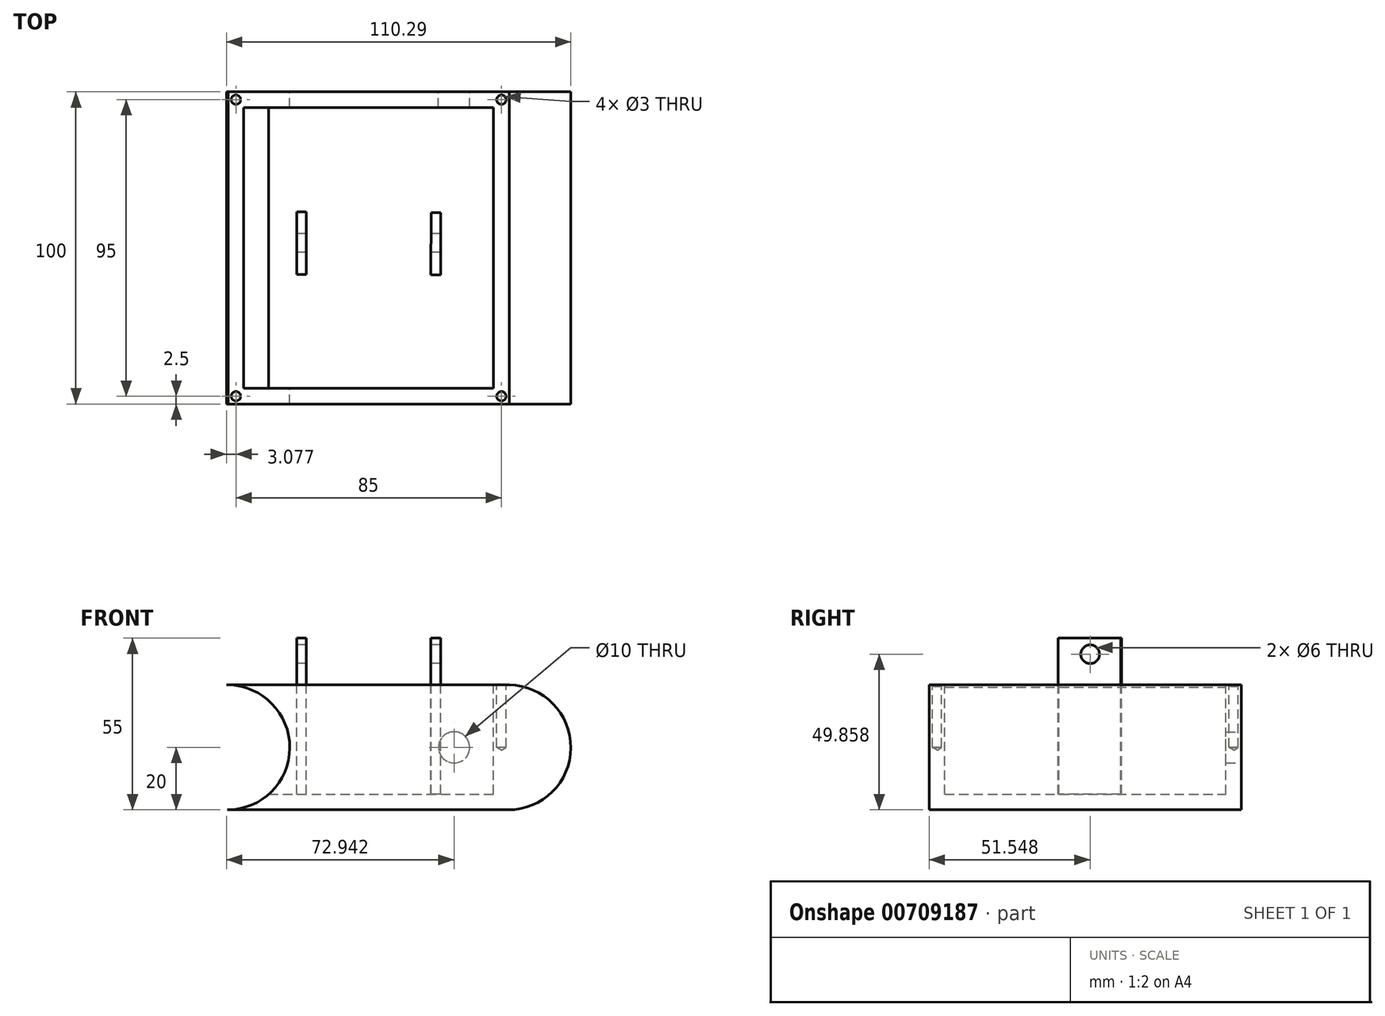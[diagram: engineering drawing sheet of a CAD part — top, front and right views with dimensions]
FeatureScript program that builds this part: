
annotation { "Feature Type Name" : "Feature", "Feature Type Description" : "" }
export const myFeature = defineFeature(function(context is Context, id is Id, definition is map)
    precondition{}
    {
        {
            var Q0;
            Q0=qCreatedBy(makeId("Front.planeOp"),FACE);
            var sketch = newSketch(context, id + "F0", { "sketchPlane" : qUnion([Q0])});
            skCircle(sketch, "E0", {"center": v(-60, 0) * mm, "radius": 20 * mm});
            skCircle(sketch, "E1", {"center": v(30, 0) * mm, "radius": 20 * mm});
            skLineSegment(sketch, "E2.top", {"start": v(-60.29, 20) * mm, "end": v(30.29, 20) * mm});
            skLineSegment(sketch, "E3", {"start": v(-60, -20) * mm, "end": v(30, -20) * mm});
            skSolve(sketch);
        }
        {
            var Q0;
            {var subQ0=sQuery(id+"F0.wireOp",EDGE,"E0");var subQ1=makeQuery(id+"F0.imprint","INTERSECT",VERTEX,{"derivedFrom":[subQ0,sQuery(id+"F0.wireOp",EDGE,"E2.top")]});Q0=makeQuery(id+"F0.imprint","IMPRINT",FACE,{"disambiguationData":[TD([[makeQuery(id+"F0.imprint","IMPRINT",EDGE,{"disambiguationData":[TD([[subQ1,-1.0]])],"derivedFrom":subQ0}),1.0]])]});}
            var Q1;
            {var subQ0=sQuery(id+"F0.wireOp",EDGE,"E1");var subQ1=makeQuery(id+"F0.imprint","INTERSECT",VERTEX,{"derivedFrom":[subQ0,sQuery(id+"F0.wireOp",EDGE,"3f78844c-1957-4825-8c51-001e57db5ed20.MirrorCS")]});Q1=makeQuery(id+"F0.imprint","IMPRINT",FACE,{"disambiguationData":[TD([[makeQuery(id+"F0.imprint","IMPRINT",EDGE,{"disambiguationData":[TD([[subQ1,1.0]])],"derivedFrom":subQ0}),1.0]])]});}
            var Q2;
            {var subQ3=sQuery(id+"F0.wireOp",EDGE,"E3");Q2=makeQuery(id+"F0.imprint","IMPRINT",FACE,{"disambiguationData":[TD([[makeQuery(id+"F0.imprint","IMPRINT",EDGE,{"derivedFrom":subQ3}),1.0]])]});}
            var Q3;
            {var subQ0=sQuery(id+"F0.wireOp",EDGE,"E2.top");var subQ1=sQuery(id+"F0.wireOp",EDGE,"E0");var subQ2=makeQuery(id+"F0.imprint","INTERSECT",VERTEX,{"disambiguationData":[OD(0.0)],"derivedFrom":[subQ1,subQ0]});Q3=makeQuery(id+"F0.imprint","IMPRINT",FACE,{"disambiguationData":[TD([[makeQuery(id+"F0.imprint","IMPRINT",EDGE,{"disambiguationData":[TD([[subQ2,-1.0]])],"derivedFrom":subQ1}),1.0]])]});}
            extrude(context, id + "F1", {"entities" : qUnion([Q0, Q1, Q2, Q3]), "endBound" : BoundingType.SYMMETRIC, "depth" : 100 * mm, "offsetDistance" : 25 * mm});
        }
        {
            var Q0;
            Q0=makeQuery(id+"F1.opExtrude","SWEPT_FACE",FACE,{"disambiguationData":[OSD([sQuery(id+"F0.wireOp",EDGE,"E2.top")])]});
            var sketch = newSketch(context, id + "F2", { "sketchPlane" : qUnion([Q0])});
            skLineSegment(sketch, "E4.bottom", {"start": v(-59.71, 50) * mm, "end": v(30.29, 50) * mm});
            skLineSegment(sketch, "E4.top", {"start": v(-59.71, -50) * mm, "end": v(30.29, -50) * mm});
            skLineSegment(sketch, "E4.left", {"start": v(-59.71, 50) * mm, "end": v(-59.71, -50) * mm});
            skLineSegment(sketch, "E4.right", {"start": v(30.29, 50) * mm, "end": v(30.29, -50) * mm});
            skLineSegment(sketch, "E5.bottom", {"start": v(-54.71, 45) * mm, "end": v(25.29, 45) * mm});
            skLineSegment(sketch, "E5.top", {"start": v(-54.71, -45) * mm, "end": v(25.29, -45) * mm});
            skLineSegment(sketch, "E5.left", {"start": v(-54.71, 45) * mm, "end": v(-54.71, -45) * mm});
            skLineSegment(sketch, "E5.right", {"start": v(25.29, 45) * mm, "end": v(25.29, -45) * mm});
            skLineSegment(sketch, "E6", {"start": v(-59.71, 50) * mm, "end": v(-54.71, 45) * mm});
            skLineSegment(sketch, "E7", {"start": v(-54.71, -45) * mm, "end": v(-59.71, -50) * mm});
            skLineSegment(sketch, "E8", {"start": v(25.29, -45) * mm, "end": v(30.29, -50) * mm});
            skLineSegment(sketch, "E9", {"start": v(25.29, 45) * mm, "end": v(30.29, 50) * mm});
            skPoint(sketch, "E10", {"position": v(-57.21, 47.5) * mm});
            skPoint(sketch, "E11", {"position": v(27.79, 47.5) * mm});
            skPoint(sketch, "E12", {"position": v(27.79, -47.5) * mm});
            skPoint(sketch, "E13", {"position": v(-57.21, -47.5) * mm});
            skLineSegment(sketch, "E14.bottom", {"start": v(-37.71, 11.55) * mm, "end": v(-34.71, 11.55) * mm});
            skLineSegment(sketch, "E14.top", {"start": v(-37.71, -8.45) * mm, "end": v(-34.71, -8.45) * mm});
            skLineSegment(sketch, "E14.left", {"start": v(-37.71, 11.55) * mm, "end": v(-37.71, -8.45) * mm});
            skLineSegment(sketch, "E14.right", {"start": v(-34.71, 11.55) * mm, "end": v(-34.71, -8.45) * mm});
            skPoint(sketch, "E15.endSnap0", {"position": v(-14.71, -45) * mm});
            skLineSegment(sketch, "E16.MirrorCS", {"start": v(8.29, -8.67) * mm, "end": v(5.13, -8.64) * mm});
            skLineSegment(sketch, "E17.MirrorCS", {"start": v(8.29, 11.33) * mm, "end": v(8.29, -8.67) * mm});
            skLineSegment(sketch, "E18.MirrorCS", {"start": v(8.29, 11.33) * mm, "end": v(5.29, 11.36) * mm});
            skLineSegment(sketch, "E19.MirrorCS", {"start": v(5.29, 11.36) * mm, "end": v(5.13, -8.64) * mm});
            skSolve(sketch);
        }
        {
            var Q0;
            Q0=makeQuery(id+"F2.imprint","IMPRINT",FACE,{"disambiguationData":[TD([[makeQuery(id+"F2.imprint","IMPRINT",EDGE,{"derivedFrom":sQuery(id+"F2.wireOp",EDGE,"E5.bottom")}),-1.0]])]});
            extrude(context, id + "F3", {"entities" : qUnion([Q0]), "operationType" : NewBodyOperationType.REMOVE, "oppositeDirection" : true, "depth" : 35 * mm, "offsetDistance" : 25 * mm});
        }
        {
            var Q0;
            Q0=sQuery(id+"F2.wireOp",VERTEX,"E10");
            var Q1;
            Q1=sQuery(id+"F2.wireOp",VERTEX,"E11");
            var Q2;
            Q2=sQuery(id+"F2.wireOp",VERTEX,"E12");
            var Q3;
            Q3=sQuery(id+"F2.wireOp",VERTEX,"E13");
            var Q4;
            Q4=makeQuery(id+"F1.opExtrude","SWEPT_BODY",BODY,{"disambiguationData":[OSD([sQuery(id+"F0.wireOp",EDGE,"E0"),sQuery(id+"F0.wireOp",EDGE,"E1"),sQuery(id+"F0.wireOp",EDGE,"E2.top"),sQuery(id+"F0.wireOp",EDGE,"E3")])]});
            hole(context, id + "F4", {"style" : HoleStyle.SIMPLE, "endStyle" : HoleEndStyle.BLIND, "holeDiameter" : 3 * mm, "majorDiameter" : 5 * mm, "holeDepth" : 20 * mm, "isTappedThrough" : true, "tappedDepth" : 12 * mm, "tapClearance" : 3, "locations" : qUnion([Q0, Q1, Q2, Q3]), "scope" : qUnion([Q4])});
        }
        {
            var Q0;
            Q0=makeQuery(id+"F1.opExtrude","CAP_FACE",FACE,{"disambiguationData":[OSD([sQuery(id+"F0.wireOp",EDGE,"E0"),sQuery(id+"F0.wireOp",EDGE,"E1"),sQuery(id+"F0.wireOp",EDGE,"E2.top"),sQuery(id+"F0.wireOp",EDGE,"E3")])],"isStart":true});
            var sketch = newSketch(context, id + "F5", { "sketchPlane" : qUnion([Q0])});
            skCircle(sketch, "E20", {"center": v(-12.65, 0) * mm, "radius": 5 * mm});
            skSolve(sketch);
        }
        {
            var Q0;
            Q0=makeQuery(id+"F5.imprint","IMPRINT",FACE,{"disambiguationData":[TD([[makeQuery(id+"F5.imprint","IMPRINT",EDGE,{"derivedFrom":sQuery(id+"F5.wireOp",EDGE,"E20")}),1.0]])]});
            extrude(context, id + "F6", {"entities" : qUnion([Q0]), "operationType" : NewBodyOperationType.REMOVE, "oppositeDirection" : true, "depth" : 10 * mm, "offsetDistance" : 25 * mm});
        }
        {
            var Q0;
            Q0=makeQuery(id+"F3.boolean.opBoolean","SPLIT",FACE,{"disambiguationData":[TD([makeQuery(id+"F3.opExtrude","SWEPT_FACE",FACE,{"disambiguationData":[OSD([sQuery(id+"F2.wireOp",EDGE,"E14.bottom")])]})])],"derivedFrom":makeQuery(id+"F1.opExtrude","SWEPT_FACE",FACE,{"disambiguationData":[OSD([sQuery(id+"F0.wireOp",EDGE,"E2.top")])]})});
            var Q1;
            Q1=makeQuery(id+"F3.boolean.opBoolean","SPLIT",FACE,{"disambiguationData":[TD([makeQuery(id+"F3.opExtrude","SWEPT_FACE",FACE,{"disambiguationData":[OSD([sQuery(id+"F2.wireOp",EDGE,"E16.MirrorCS")])]})])],"derivedFrom":makeQuery(id+"F1.opExtrude","SWEPT_FACE",FACE,{"disambiguationData":[OSD([sQuery(id+"F0.wireOp",EDGE,"E2.top")])]})});
            extrude(context, id + "F7", {"entities" : qUnion([Q0, Q1]), "operationType" : NewBodyOperationType.ADD, "depth" : 15 * mm, "offsetDistance" : 25 * mm});
        }
        {
            var Q0;
            {var subQ0=sQuery(id+"F2.wireOp",EDGE,"E14.left");Q0=makeQuery(id+"F7.boolean.opBoolean","MERGE",FACE,{"derivedFrom":[makeQuery(id+"F3.boolean.opBoolean","COPY",FACE,{"derivedFrom":makeQuery(id+"F3.opExtrude","SWEPT_FACE",FACE,{"disambiguationData":[OSD([subQ0])]})}),makeQuery(id+"F7.opExtrude","SWEPT_FACE",FACE,{"disambiguationData":[OSD([subQ0])]})]});}
            var sketch = newSketch(context, id + "F8", { "sketchPlane" : qUnion([Q0])});
            skCircle(sketch, "E21", {"center": v(-1.55, 29.86) * mm, "radius": 3 * mm});
            skSolve(sketch);
        }
        {
            var Q0;
            Q0=makeQuery(id+"F8.imprint","IMPRINT",FACE,{"disambiguationData":[TD([[makeQuery(id+"F8.imprint","IMPRINT",EDGE,{"derivedFrom":sQuery(id+"F8.wireOp",EDGE,"E21")}),1.0]])]});
            extrude(context, id + "F9", {"entities" : qUnion([Q0]), "operationType" : NewBodyOperationType.REMOVE, "oppositeDirection" : true, "depth" : 60 * mm, "offsetDistance" : 25 * mm});
        }
    });
